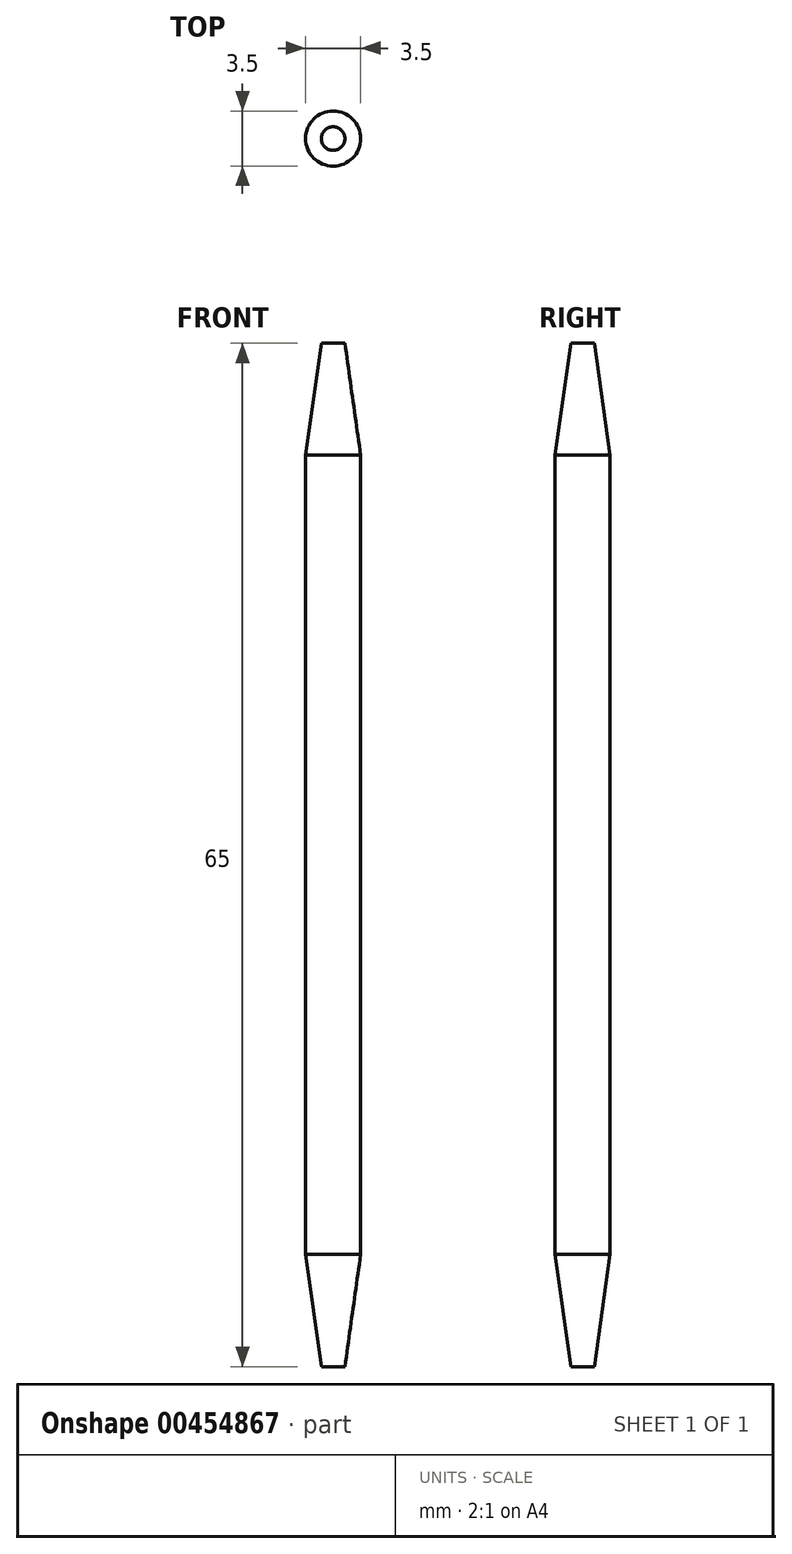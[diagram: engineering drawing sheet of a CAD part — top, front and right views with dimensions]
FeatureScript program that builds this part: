
annotation { "Feature Type Name" : "Feature", "Feature Type Description" : "" }
export const myFeature = defineFeature(function(context is Context, id is Id, definition is map)
    precondition{}
    {
        {
            var Q0;
            Q0=qCreatedBy(makeId("Top.planeOp"),FACE);
            var sketch = newSketch(context, id + "F0", { "sketchPlane" : qUnion([Q0])});
            skCircle(sketch, "E0", {"center": v(0, 0) * mm, "radius": 1.75 * mm});
            skSolve(sketch);
        }
        {
            var Q0;
            Q0 = qSketchRegion(id + "F0", true);
            extrude(context, id + "F1", {"entities" : qUnion([Q0]), "depth" : 50 * mm});
        }
        {
            var Q0;
            Q0=makeQuery(id+"F1.opExtrude","CAP_FACE",FACE,{"disambiguationData":[OSD([sQuery(id+"F0.wireOp",EDGE,"E0")])],"isStart":false});
            var sketch = newSketch(context, id + "F2", { "sketchPlane" : qUnion([Q0])});
            skCircle(sketch, "E1", {"center": v(0, 0) * mm, "radius": 1.75 * mm});
            skSolve(sketch);
        }
        {
            var Q0;
            Q0 = qSketchRegion(id + "F2", true);
            extrude(context, id + "F3", {"entities" : qUnion([Q0]), "operationType" : NewBodyOperationType.ADD, "depth" : 7.5 * mm});
        }
        {
            var Q0;
            Q0=makeQuery(id+"F3.opExtrude","CAP_EDGE",EDGE,{"disambiguationData":[OSD([sQuery(id+"F2.wireOp",EDGE,"E1")])],"isStart":false});
            chamfer(context, id + "F4", {"entities" : qUnion([Q0]), "chamferType" : ChamferType.OFFSET_ANGLE, "width" : 1 * mm, "oppositeDirection" : false, "angle" : 82 * degree, "tangentPropagation" : true});
        }
        {
            var Q0;
            Q0=makeQuery(id+"F1.opExtrude","CAP_FACE",FACE,{"disambiguationData":[OSD([sQuery(id+"F0.wireOp",EDGE,"E0")])],"isStart":true});
            extrude(context, id + "F5", {"entities" : qUnion([Q0]), "operationType" : NewBodyOperationType.ADD, "depth" : 7.5 * mm});
        }
        {
            var Q0;
            Q0=makeQuery(id+"F5.opExtrude","CAP_EDGE",EDGE,{"disambiguationData":[OSD([sQuery(id+"F0.wireOp",EDGE,"E0")])],"isStart":false});
            chamfer(context, id + "F6", {"entities" : qUnion([Q0]), "chamferType" : ChamferType.OFFSET_ANGLE, "width" : 1 * mm, "oppositeDirection" : true, "angle" : 82 * degree, "tangentPropagation" : true});
        }
    });
